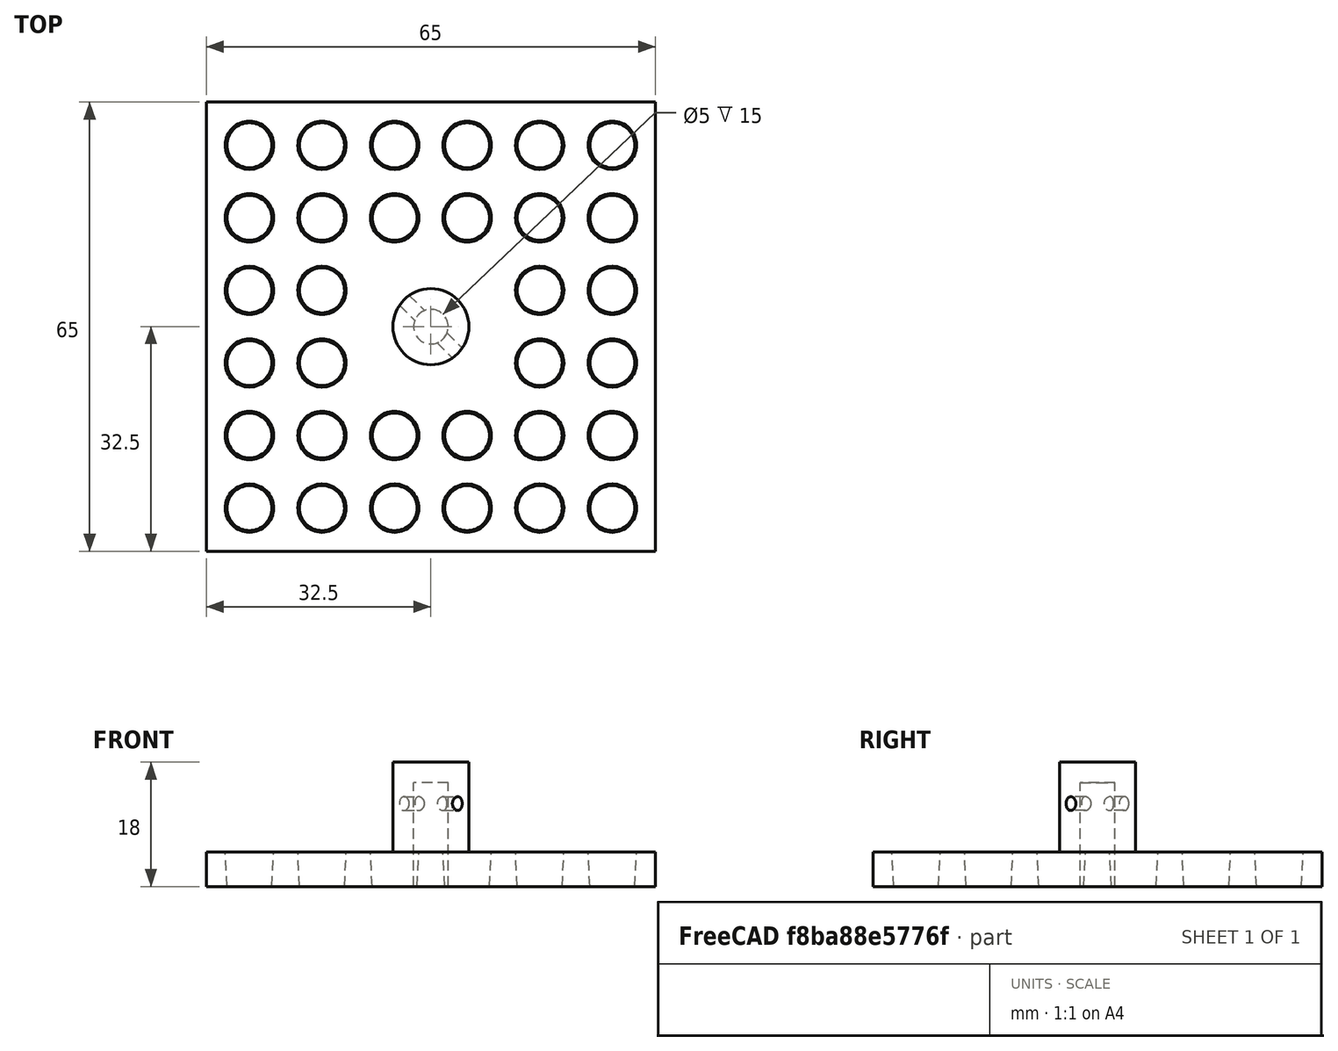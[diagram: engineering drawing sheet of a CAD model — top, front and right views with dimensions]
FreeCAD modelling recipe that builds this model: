
FCSTD DOCUMENT  (FreeCAD 0.17R13541 (Git))
Label: tip-changer-top
License: All rights reserved
LicenseURL: http://en.wikipedia.org/wiki/All_rights_reserved
objects: Part::Cut×34, Part::Cone×32, Part::Cylinder×4, Part::MultiFuse×2, Part::Box×1, Spreadsheet::Sheet×1, Mesh::Feature×1
note: 73 computed .brp shape members not serialized (recipe doc carries the construction recipe); baked Part::Feature solids carry a one-line shape summary decoded from their .brp

FEATURE [Part::Cone] Cone019  label="Kegel019"
  Angle = 360
  AttacherType = Attacher::AttachEngine3D
  Height = 5
  Placement = pos=(-5.25,15.75,78) rot=(0,0,1;0rad)
  Radius1 = 3.25
  Radius2 = 3.5
  expr: Placement.Base.y = Tabelle1.B6 / 2 - Tabelle1.B39 - Tabelle1.B37
  expr: Placement.Base.x = Tabelle1.B6 / 2 - Tabelle1.B39 - Tabelle1.B37 * 3
  expr: Placement.Base.z = Tabelle1.B33 + Tabelle1.B14
  expr: Radius2 = Tabelle1.B35 / 2
  expr: Radius1 = Tabelle1.B36 / 2
FEATURE [Part::Cylinder] Cylinder028  label="Zylinder026"
  Angle = 360
  AttacherType = Attacher::AttachEngine3D
  Height = 15
  Placement = pos=(-6,6,90) rot=(0.862856,0.357407,0.357407;1.71777rad)
  Radius = 1
FEATURE [Part::Cone] Cone018  label="Kegel018"
  Angle = 360
  AttacherType = Attacher::AttachEngine3D
  Height = 5
  Placement = pos=(5.25,26.25,78) rot=(0,0,1;0rad)
  Radius1 = 3.25
  Radius2 = 3.5
  expr: Placement.Base.y = Tabelle1.B6 / 2 - Tabelle1.B39
  expr: Placement.Base.x = Tabelle1.B6 / 2 - Tabelle1.B39 - Tabelle1.B37 * 2
  expr: Placement.Base.z = Tabelle1.B33 + Tabelle1.B14
  expr: Radius2 = Tabelle1.B35 / 2
  expr: Radius1 = Tabelle1.B36 / 2
FEATURE [Part::Cylinder] Cylinder027  label="Zylinder025"
  Angle = 360
  AttacherType = Attacher::AttachEngine3D
  Height = 3
  Placement = pos=(0,0,93) rot=(0,0,1;0rad)
  Radius = 5.5
FEATURE [Part::Cone] Cone022  label="Kegel022"
  Angle = 360
  AttacherType = Attacher::AttachEngine3D
  Height = 5
  Placement = pos=(15.75,-26.25,78) rot=(0,0,1;0rad)
  Radius1 = 3.25
  Radius2 = 3.5
  expr: Placement.Base.y = Tabelle1.B6 / 2 - Tabelle1.B39 - Tabelle1.B37 * 5
  expr: Placement.Base.x = Tabelle1.B6 / 2 - Tabelle1.B39 - Tabelle1.B37 * 1
  expr: Placement.Base.z = Tabelle1.B33 + Tabelle1.B14
  expr: Radius2 = Tabelle1.B35 / 2
  expr: Radius1 = Tabelle1.B36 / 2
FEATURE [Part::Cone] Cone021  label="Kegel021"
  Angle = 360
  AttacherType = Attacher::AttachEngine3D
  Height = 5
  Placement = pos=(5.25,-26.25,78) rot=(0,0,1;0rad)
  Radius1 = 3.25
  Radius2 = 3.5
  expr: Placement.Base.y = Tabelle1.B6 / 2 - Tabelle1.B39 - Tabelle1.B37 * 5
  expr: Placement.Base.x = Tabelle1.B6 / 2 - Tabelle1.B39 - Tabelle1.B37 * 2
  expr: Placement.Base.z = Tabelle1.B33 + Tabelle1.B14
  expr: Radius2 = Tabelle1.B35 / 2
  expr: Radius1 = Tabelle1.B36 / 2
FEATURE [Part::Cone] Cone023  label="Kegel023"
  Angle = 360
  AttacherType = Attacher::AttachEngine3D
  Height = 5
  Placement = pos=(26.25,-26.25,78) rot=(0,0,1;0rad)
  Radius1 = 3.25
  Radius2 = 3.5
  expr: Placement.Base.y = Tabelle1.B6 / 2 - Tabelle1.B39 - Tabelle1.B37 * 5
  expr: Placement.Base.x = Tabelle1.B6 / 2 - Tabelle1.B39 - Tabelle1.B37 * 0
  expr: Placement.Base.z = Tabelle1.B33 + Tabelle1.B14
  expr: Radius2 = Tabelle1.B35 / 2
  expr: Radius1 = Tabelle1.B36 / 2
FEATURE [Part::Cylinder] Cylinder020  label="Spindel001"
  Angle = 360
  AttacherType = Attacher::AttachEngine3D
  Height = 60
  Placement = pos=(0,0,33) rot=(0,0,1;0rad)
  Radius = 2.5
  expr: Placement.Base.z = Tabelle1.B33 + Tabelle1.B14 - Tabelle1.B15 + Tabelle1.B12
  expr: Height = Tabelle1.B15
FEATURE [Part::Cone] Cone020  label="Kegel020"
  Angle = 360
  AttacherType = Attacher::AttachEngine3D
  Height = 5
  Placement = pos=(5.25,15.75,78) rot=(0,0,1;0rad)
  Radius1 = 3.25
  Radius2 = 3.5
  expr: Placement.Base.y = Tabelle1.B6 / 2 - Tabelle1.B39 - Tabelle1.B37
  expr: Placement.Base.x = Tabelle1.B6 / 2 - Tabelle1.B39 - Tabelle1.B37 * 2
  expr: Placement.Base.z = Tabelle1.B33 + Tabelle1.B14
  expr: Radius2 = Tabelle1.B35 / 2
  expr: Radius1 = Tabelle1.B36 / 2
FEATURE [Part::Cone] Cone024  label="Kegel024"
  Angle = 360
  AttacherType = Attacher::AttachEngine3D
  Height = 5
  Placement = pos=(-5.25,-26.25,78) rot=(0,0,1;0rad)
  Radius1 = 3.25
  Radius2 = 3.5
  expr: Placement.Base.y = Tabelle1.B6 / 2 - Tabelle1.B39 - Tabelle1.B37 * 5
  expr: Placement.Base.x = Tabelle1.B6 / 2 - Tabelle1.B39 - Tabelle1.B37 * 3
  expr: Placement.Base.z = Tabelle1.B33 + Tabelle1.B14
  expr: Radius2 = Tabelle1.B35 / 2
  expr: Radius1 = Tabelle1.B36 / 2
FEATURE [Part::Cone] Cone029  label="Kegel029"
  Angle = 360
  AttacherType = Attacher::AttachEngine3D
  Height = 5
  Placement = pos=(-26.25,5.25,78) rot=(0,0,1;0rad)
  Radius1 = 3.25
  Radius2 = 3.5
  expr: Placement.Base.y = Tabelle1.B6 / 2 - Tabelle1.B39 - Tabelle1.B37 * 2
  expr: Placement.Base.x = Tabelle1.B6 / 2 - Tabelle1.B39 - Tabelle1.B37 * 5
  expr: Placement.Base.z = Tabelle1.B33 + Tabelle1.B14
  expr: Radius2 = Tabelle1.B35 / 2
  expr: Radius1 = Tabelle1.B36 / 2
FEATURE [Part::Cone] Cone030  label="Kegel030"
  Angle = 360
  AttacherType = Attacher::AttachEngine3D
  Height = 5
  Placement = pos=(-26.25,15.75,78) rot=(0,0,1;0rad)
  Radius1 = 3.25
  Radius2 = 3.5
  expr: Placement.Base.y = Tabelle1.B6 / 2 - Tabelle1.B39 - Tabelle1.B37 * 1
  expr: Placement.Base.x = Tabelle1.B6 / 2 - Tabelle1.B39 - Tabelle1.B37 * 5
  expr: Placement.Base.z = Tabelle1.B33 + Tabelle1.B14
  expr: Radius2 = Tabelle1.B35 / 2
  expr: Radius1 = Tabelle1.B36 / 2
FEATURE [Part::Cone] Cone027  label="Kegel027"
  Angle = 360
  AttacherType = Attacher::AttachEngine3D
  Height = 5
  Placement = pos=(-26.25,-15.75,78) rot=(0,0,1;0rad)
  Radius1 = 3.25
  Radius2 = 3.5
  expr: Placement.Base.y = Tabelle1.B6 / 2 - Tabelle1.B39 - Tabelle1.B37 * 4
  expr: Placement.Base.x = Tabelle1.B6 / 2 - Tabelle1.B39 - Tabelle1.B37 * 5
  expr: Placement.Base.z = Tabelle1.B33 + Tabelle1.B14
  expr: Radius2 = Tabelle1.B35 / 2
  expr: Radius1 = Tabelle1.B36 / 2
FEATURE [Part::Cone] Cone025  label="Kegel025"
  Angle = 360
  AttacherType = Attacher::AttachEngine3D
  Height = 5
  Placement = pos=(-15.75,-26.25,78) rot=(0,0,1;0rad)
  Radius1 = 3.25
  Radius2 = 3.5
  expr: Placement.Base.y = Tabelle1.B6 / 2 - Tabelle1.B39 - Tabelle1.B37 * 5
  expr: Placement.Base.x = Tabelle1.B6 / 2 - Tabelle1.B39 - Tabelle1.B37 * 4
  expr: Placement.Base.z = Tabelle1.B33 + Tabelle1.B14
  expr: Radius2 = Tabelle1.B35 / 2
  expr: Radius1 = Tabelle1.B36 / 2
FEATURE [Part::Cone] Cone028  label="Kegel028"
  Angle = 360
  AttacherType = Attacher::AttachEngine3D
  Height = 5
  Placement = pos=(-26.25,-5.25,78) rot=(0,0,1;0rad)
  Radius1 = 3.25
  Radius2 = 3.5
  expr: Placement.Base.y = Tabelle1.B6 / 2 - Tabelle1.B39 - Tabelle1.B37 * 3
  expr: Placement.Base.x = Tabelle1.B6 / 2 - Tabelle1.B39 - Tabelle1.B37 * 5
  expr: Placement.Base.z = Tabelle1.B33 + Tabelle1.B14
  expr: Radius2 = Tabelle1.B35 / 2
  expr: Radius1 = Tabelle1.B36 / 2
FEATURE [Part::Cone] Cone031  label="Kegel031"
  Angle = 360
  AttacherType = Attacher::AttachEngine3D
  Height = 5
  Placement = pos=(-26.25,26.25,78) rot=(0,0,1;0rad)
  Radius1 = 3.25
  Radius2 = 3.5
  expr: Placement.Base.y = Tabelle1.B6 / 2 - Tabelle1.B39 - Tabelle1.B37 * 0
  expr: Placement.Base.x = Tabelle1.B6 / 2 - Tabelle1.B39 - Tabelle1.B37 * 5
  expr: Placement.Base.z = Tabelle1.B33 + Tabelle1.B14
  expr: Radius2 = Tabelle1.B35 / 2
  expr: Radius1 = Tabelle1.B36 / 2
FEATURE [Part::Cone] Cone026  label="Kegel026"
  Angle = 360
  AttacherType = Attacher::AttachEngine3D
  Height = 5
  Placement = pos=(-26.25,-26.25,78) rot=(0,0,1;0rad)
  Radius1 = 3.25
  Radius2 = 3.5
  expr: Placement.Base.y = Tabelle1.B6 / 2 - Tabelle1.B39 - Tabelle1.B37 * 5
  expr: Placement.Base.x = Tabelle1.B6 / 2 - Tabelle1.B39 - Tabelle1.B37 * 5
  expr: Placement.Base.z = Tabelle1.B33 + Tabelle1.B14
  expr: Radius2 = Tabelle1.B35 / 2
  expr: Radius1 = Tabelle1.B36 / 2
FEATURE [Part::Cone] Cone014  label="Kegel014"
  Angle = 360
  AttacherType = Attacher::AttachEngine3D
  Height = 5
  Placement = pos=(-15.75,5.25,78) rot=(0,0,1;0rad)
  Radius1 = 3.25
  Radius2 = 3.5
  expr: Placement.Base.y = Tabelle1.B6 / 2 - Tabelle1.B39 - Tabelle1.B37 * 2
  expr: Placement.Base.x = Tabelle1.B6 / 2 - Tabelle1.B39 - Tabelle1.B37 * 4
  expr: Placement.Base.z = Tabelle1.B33 + Tabelle1.B14
  expr: Radius2 = Tabelle1.B35 / 2
  expr: Radius1 = Tabelle1.B36 / 2
FEATURE [Part::Cone] Cone001  label="Kegel001"
  Angle = 360
  AttacherType = Attacher::AttachEngine3D
  Height = 5
  Placement = pos=(26.25,15.75,78) rot=(0,0,1;0rad)
  Radius1 = 3.25
  Radius2 = 3.5
  expr: Placement.Base.y = Tabelle1.B6 / 2 - Tabelle1.B39 - Tabelle1.B37
  expr: Placement.Base.x = Tabelle1.B6 / 2 - Tabelle1.B39
  expr: Placement.Base.z = Tabelle1.B33 + Tabelle1.B14
  expr: Radius2 = Tabelle1.B35 / 2
  expr: Radius1 = Tabelle1.B36 / 2
FEATURE [Part::Cone] Cone015  label="Kegel015"
  Angle = 360
  AttacherType = Attacher::AttachEngine3D
  Height = 5
  Placement = pos=(-15.75,15.75,78) rot=(0,0,1;0rad)
  Radius1 = 3.25
  Radius2 = 3.5
  expr: Placement.Base.y = Tabelle1.B6 / 2 - Tabelle1.B39 - Tabelle1.B37
  expr: Placement.Base.x = Tabelle1.B6 / 2 - Tabelle1.B39 - Tabelle1.B37 * 4
  expr: Placement.Base.z = Tabelle1.B33 + Tabelle1.B14
  expr: Radius2 = Tabelle1.B35 / 2
  expr: Radius1 = Tabelle1.B36 / 2
FEATURE [Part::Box] Box001  label="Platte"
  AttacherType = Attacher::AttachEngine3D
  Height = 5
  Length = 65
  Placement = pos=(-32.5,-32.5,78) rot=(0,0,1;0rad)
  Width = 65
  expr: Length = Tabelle1.B6
  expr: Placement.Base.z = Tabelle1.B33 + Tabelle1.B14
  expr: Placement.Base.y = -Tabelle1.B6 / 2
  expr: Placement.Base.x = -Tabelle1.B6 / 2
  expr: Width = Tabelle1.B6
FEATURE [Part::Cone] Cone006  label="Kegel006"
  Angle = 360
  AttacherType = Attacher::AttachEngine3D
  Height = 5
  Placement = pos=(15.75,-5.25,78) rot=(0,0,1;0rad)
  Radius1 = 3.25
  Radius2 = 3.5
  expr: Placement.Base.y = Tabelle1.B6 / 2 - Tabelle1.B39 - Tabelle1.B37 * 3
  expr: Placement.Base.x = Tabelle1.B6 / 2 - Tabelle1.B39 - Tabelle1.B37
  expr: Placement.Base.z = Tabelle1.B33 + Tabelle1.B14
  expr: Radius2 = Tabelle1.B35 / 2
  expr: Radius1 = Tabelle1.B36 / 2
FEATURE [Part::Cone] Cone016  label="Kegel016"
  Angle = 360
  AttacherType = Attacher::AttachEngine3D
  Height = 5
  Placement = pos=(-15.75,26.25,78) rot=(0,0,1;0rad)
  Radius1 = 3.25
  Radius2 = 3.5
  expr: Placement.Base.y = Tabelle1.B6 / 2 - Tabelle1.B39
  expr: Placement.Base.x = Tabelle1.B6 / 2 - Tabelle1.B39 - Tabelle1.B37 * 4
  expr: Placement.Base.z = Tabelle1.B33 + Tabelle1.B14
  expr: Radius2 = Tabelle1.B35 / 2
  expr: Radius1 = Tabelle1.B36 / 2
FEATURE [Part::Cone] Cone010  label="Kegel010"
  Angle = 360
  AttacherType = Attacher::AttachEngine3D
  Height = 5
  Placement = pos=(5.25,-15.75,78) rot=(0,0,1;0rad)
  Radius1 = 3.25
  Radius2 = 3.5
  expr: Placement.Base.y = Tabelle1.B6 / 2 - Tabelle1.B39 - Tabelle1.B37 * 4
  expr: Placement.Base.x = Tabelle1.B6 / 2 - Tabelle1.B39 - Tabelle1.B37 * 2
  expr: Placement.Base.z = Tabelle1.B33 + Tabelle1.B14
  expr: Radius2 = Tabelle1.B35 / 2
  expr: Radius1 = Tabelle1.B36 / 2
FEATURE [Part::Cylinder] Cylinder019  label="Zylinder018"
  Angle = 360
  AttacherType = Attacher::AttachEngine3D
  Height = 10
  Placement = pos=(0,0,83) rot=(0,0,1;0rad)
  Radius = 5.5
  expr: Placement.Base.z = Tabelle1.B33 + Tabelle1.B14 + Tabelle1.B7
  expr: Height = Tabelle1.B8
  expr: Radius = Tabelle1.B11 / 2 + Tabelle1.B19
FEATURE [Part::Cone] Cone011  label="Kegel011"
  Angle = 360
  AttacherType = Attacher::AttachEngine3D
  Height = 5
  Placement = pos=(-5.25,-15.75,78) rot=(0,0,1;0rad)
  Radius1 = 3.25
  Radius2 = 3.5
  expr: Placement.Base.y = Tabelle1.B6 / 2 - Tabelle1.B39 - Tabelle1.B37 * 4
  expr: Placement.Base.x = Tabelle1.B6 / 2 - Tabelle1.B39 - Tabelle1.B37 * 3
  expr: Placement.Base.z = Tabelle1.B33 + Tabelle1.B14
  expr: Radius2 = Tabelle1.B35 / 2
  expr: Radius1 = Tabelle1.B36 / 2
FEATURE [Part::Cone] Cone017  label="Kegel017"
  Angle = 360
  AttacherType = Attacher::AttachEngine3D
  Height = 5
  Placement = pos=(-5.25,26.25,78) rot=(0,0,1;0rad)
  Radius1 = 3.25
  Radius2 = 3.5
  expr: Placement.Base.y = Tabelle1.B6 / 2 - Tabelle1.B39
  expr: Placement.Base.x = Tabelle1.B6 / 2 - Tabelle1.B39 - Tabelle1.B37 * 3
  expr: Placement.Base.z = Tabelle1.B33 + Tabelle1.B14
  expr: Radius2 = Tabelle1.B35 / 2
  expr: Radius1 = Tabelle1.B36 / 2
FEATURE [Part::Cone] Cone007  label="Kegel007"
  Angle = 360
  AttacherType = Attacher::AttachEngine3D
  Height = 5
  Placement = pos=(15.75,5.25,78) rot=(0,0,1;0rad)
  Radius1 = 3.25
  Radius2 = 3.5
  expr: Placement.Base.y = Tabelle1.B6 / 2 - Tabelle1.B39 - Tabelle1.B37 * 2
  expr: Placement.Base.x = Tabelle1.B6 / 2 - Tabelle1.B39 - Tabelle1.B37
  expr: Placement.Base.z = Tabelle1.B33 + Tabelle1.B14
  expr: Radius2 = Tabelle1.B35 / 2
  expr: Radius1 = Tabelle1.B36 / 2
FEATURE [Part::Cone] Cone008  label="Kegel008"
  Angle = 360
  AttacherType = Attacher::AttachEngine3D
  Height = 5
  Placement = pos=(15.75,15.75,78) rot=(0,0,1;0rad)
  Radius1 = 3.25
  Radius2 = 3.5
  expr: Placement.Base.y = Tabelle1.B6 / 2 - Tabelle1.B39 - Tabelle1.B37
  expr: Placement.Base.x = Tabelle1.B6 / 2 - Tabelle1.B39 - Tabelle1.B37
  expr: Placement.Base.z = Tabelle1.B33 + Tabelle1.B14
  expr: Radius2 = Tabelle1.B35 / 2
  expr: Radius1 = Tabelle1.B36 / 2
FEATURE [Part::Cone] Cone005  label="Kegel005"
  Angle = 360
  AttacherType = Attacher::AttachEngine3D
  Height = 5
  Placement = pos=(26.25,-15.75,78) rot=(0,0,1;0rad)
  Radius1 = 3.25
  Radius2 = 3.5
  expr: Placement.Base.y = Tabelle1.B6 / 2 - Tabelle1.B37 * 4 - Tabelle1.B39
  expr: Placement.Base.x = Tabelle1.B6 / 2 - Tabelle1.B39
  expr: Placement.Base.z = Tabelle1.B33 + Tabelle1.B14
  expr: Radius2 = Tabelle1.B35 / 2
  expr: Radius1 = Tabelle1.B36 / 2
FEATURE [Part::Cone] Cone009  label="Kegel009"
  Angle = 360
  AttacherType = Attacher::AttachEngine3D
  Height = 5
  Placement = pos=(15.75,26.25,78) rot=(0,0,1;0rad)
  Radius1 = 3.25
  Radius2 = 3.5
  expr: Placement.Base.y = Tabelle1.B6 / 2 - Tabelle1.B39
  expr: Placement.Base.x = Tabelle1.B6 / 2 - Tabelle1.B39 - Tabelle1.B37
  expr: Placement.Base.z = Tabelle1.B33 + Tabelle1.B14
  expr: Radius2 = Tabelle1.B35 / 2
  expr: Radius1 = Tabelle1.B36 / 2
FEATURE [Part::Cone] Cone013  label="Kegel013"
  Angle = 360
  AttacherType = Attacher::AttachEngine3D
  Height = 5
  Placement = pos=(-15.75,-5.25,78) rot=(0,0,1;0rad)
  Radius1 = 3.25
  Radius2 = 3.5
  expr: Placement.Base.y = Tabelle1.B6 / 2 - Tabelle1.B39 - Tabelle1.B37 * 3
  expr: Placement.Base.x = Tabelle1.B6 / 2 - Tabelle1.B39 - Tabelle1.B37 * 4
  expr: Placement.Base.z = Tabelle1.B33 + Tabelle1.B14
  expr: Radius2 = Tabelle1.B35 / 2
  expr: Radius1 = Tabelle1.B36 / 2
FEATURE [Part::Cone] Cone  label="Kegel"
  Angle = 360
  AttacherType = Attacher::AttachEngine3D
  Height = 5
  Placement = pos=(26.25,26.25,78) rot=(0,0,1;0rad)
  Radius1 = 3.25
  Radius2 = 3.5
  expr: Placement.Base.y = Tabelle1.B6 / 2 - Tabelle1.B39
  expr: Placement.Base.x = Tabelle1.B6 / 2 - Tabelle1.B39
  expr: Placement.Base.z = Tabelle1.B33 + Tabelle1.B14
  expr: Radius2 = Tabelle1.B35 / 2
  expr: Radius1 = Tabelle1.B36 / 2
FEATURE [Part::Cut] Cut008
  Base = -> Box001
  Tool = -> Cone
FEATURE [Part::Cut] Cut009
  Base = -> Cut008
  Tool = -> Cone023
FEATURE [Part::Cut] Cut010
  Base = -> Cut009
  Tool = -> Cone022
FEATURE [Part::Cut] Cut011
  Base = -> Cut010
  Tool = -> Cone021
FEATURE [Part::Cone] Cone003  label="Kegel003"
  Angle = 360
  AttacherType = Attacher::AttachEngine3D
  Height = 5
  Placement = pos=(26.25,-5.25,78) rot=(0,0,1;0rad)
  Radius1 = 3.25
  Radius2 = 3.5
  expr: Placement.Base.y = Tabelle1.B6 / 2 - Tabelle1.B39 - Tabelle1.B37 * 3
  expr: Placement.Base.x = Tabelle1.B6 / 2 - Tabelle1.B39
  expr: Placement.Base.z = Tabelle1.B33 + Tabelle1.B14
  expr: Radius2 = Tabelle1.B35 / 2
  expr: Radius1 = Tabelle1.B36 / 2
FEATURE [Part::Cone] Cone002  label="Kegel002"
  Angle = 360
  AttacherType = Attacher::AttachEngine3D
  Height = 5
  Placement = pos=(26.25,5.25,78) rot=(0,0,1;0rad)
  Radius1 = 3.25
  Radius2 = 3.5
  expr: Placement.Base.y = Tabelle1.B6 / 2 - Tabelle1.B39 - Tabelle1.B37 * 2
  expr: Placement.Base.x = Tabelle1.B6 / 2 - Tabelle1.B39
  expr: Placement.Base.z = Tabelle1.B33 + Tabelle1.B14
  expr: Radius2 = Tabelle1.B35 / 2
  expr: Radius1 = Tabelle1.B36 / 2
FEATURE [Part::Cone] Cone012  label="Kegel012"
  Angle = 360
  AttacherType = Attacher::AttachEngine3D
  Height = 5
  Placement = pos=(-15.75,-15.75,78) rot=(0,0,1;0rad)
  Radius1 = 3.25
  Radius2 = 3.5
  expr: Placement.Base.y = Tabelle1.B6 / 2 - Tabelle1.B39 - Tabelle1.B37 * 4
  expr: Placement.Base.x = Tabelle1.B6 / 2 - Tabelle1.B39 - Tabelle1.B37 * 4
  expr: Placement.Base.z = Tabelle1.B33 + Tabelle1.B14
  expr: Radius2 = Tabelle1.B35 / 2
  expr: Radius1 = Tabelle1.B36 / 2
FEATURE [Part::Cone] Cone004  label="Kegel004"
  Angle = 360
  AttacherType = Attacher::AttachEngine3D
  Height = 5
  Placement = pos=(15.75,-15.75,78) rot=(0,0,1;0rad)
  Radius1 = 3.25
  Radius2 = 3.5
  expr: Placement.Base.y = Tabelle1.B6 / 2 - Tabelle1.B39 - Tabelle1.B37 * 4
  expr: Placement.Base.x = Tabelle1.B6 / 2 - Tabelle1.B39 - Tabelle1.B37
  expr: Placement.Base.z = Tabelle1.B33 + Tabelle1.B14
  expr: Radius2 = Tabelle1.B35 / 2
  expr: Radius1 = Tabelle1.B36 / 2
FEATURE [Part::Cut] Cut012
  Base = -> Cut011
  Tool = -> Cone020
FEATURE [Part::Cut] Cut013
  Base = -> Cut012
  Tool = -> Cone019
FEATURE [Part::Cut] Cut014
  Base = -> Cut013
  Tool = -> Cone018
FEATURE [Part::Cut] Cut015
  Base = -> Cut014
  Tool = -> Cone017
FEATURE [Part::Cut] Cut016
  Base = -> Cut015
  Tool = -> Cone016
FEATURE [Part::Cut] Cut017
  Base = -> Cut016
  Tool = -> Cone015
FEATURE [Part::Cut] Cut018
  Base = -> Cut017
  Tool = -> Cone014
FEATURE [Part::Cut] Cut019
  Base = -> Cut018
  Tool = -> Cone013
FEATURE [Part::Cut] Cut020
  Base = -> Cut019
  Tool = -> Cone012
FEATURE [Part::Cut] Cut021
  Base = -> Cut020
  Tool = -> Cone011
FEATURE [Part::Cut] Cut022
  Base = -> Cut021
  Tool = -> Cone010
FEATURE [Part::Cut] Cut023
  Base = -> Cut022
  Tool = -> Cone009
FEATURE [Part::Cut] Cut024
  Base = -> Cut023
  Tool = -> Cone008
FEATURE [Part::Cut] Cut025
  Base = -> Cut024
  Tool = -> Cone007
FEATURE [Part::Cut] Cut026
  Base = -> Cut025
  Tool = -> Cone006
FEATURE [Part::Cut] Cut027
  Base = -> Cut026
  Tool = -> Cone005
FEATURE [Part::Cut] Cut028
  Base = -> Cut027
  Tool = -> Cone004
FEATURE [Part::Cut] Cut029
  Base = -> Cut028
  Tool = -> Cone003
FEATURE [Part::Cut] Cut030
  Base = -> Cut029
  Tool = -> Cone002
FEATURE [Part::Cut] Cut031
  Base = -> Cut030
  Tool = -> Cone001
FEATURE [Part::MultiFuse] Fusion
  Shapes = -> [Cut031,Cylinder019]
FEATURE [Part::Cut] Cut032
  Base = -> Fusion
  Tool = -> Cylinder020
FEATURE [Part::MultiFuse] Fusion002  label="top"
  Shapes = -> [Cut032,Cylinder027]
FEATURE [Part::Cut] Cut042  label="Top"
  Base = -> Fusion002
  Tool = -> Cylinder028
FEATURE [Part::Cut] Cut048
  Base = -> Cut042
  Tool = -> Cone024
FEATURE [Part::Cut] Cut049
  Base = -> Cut048
  Tool = -> Cone031
FEATURE [Part::Cut] Cut050
  Base = -> Cut049
  Tool = -> Cone030
FEATURE [Part::Cut] Cut051
  Base = -> Cut050
  Tool = -> Cone029
FEATURE [Part::Cut] Cut052
  Base = -> Cut051
  Tool = -> Cone028
FEATURE [Part::Cut] Cut053
  Base = -> Cut052
  Tool = -> Cone027
FEATURE [Part::Cut] Cut054
  Base = -> Cut053
  Tool = -> Cone026
FEATURE [Part::Cut] Cut055  label="tip-changer-top"
  Base = -> Cut054
  Tool = -> Cone025
FEATURE [Spreadsheet::Sheet] Tabelle1
  cells = A1=Abstand Pip/Boden; B1=65; A3=Toleranz; B3=0.20000000000000001; A5=Teller; A6=Breite/Länge; B6=65; A7=Dicke; B7=5; A8=Befestigung höhe; B8=10; A10=Achse; A11=Durchmesser; B11=5; A12=Teller Befestigung; B12==B7 + B8; A13=Führung Länge; B13=40; C13=Wandstärke; D13=5; A14=Freiraum; B14=5; A15=Länge; B15==B14 + B13 + B12; A17=Feder; A18=Hülse durchmesser; B18=3.6000000000000001; A19=Hülse Wanddicke; B19=3; A20=L0; B20=25; A21=delta L; B21=3; A22=Spannmutter; A23=Höhe; B23=10; A24=Durchmesser Pitch; B24=20; A25=min Abstand Boden; B25=5; A28=min Oberkante Platte; B28==B25 + B23 + B20 + B19 + B13 + B7; A30=Gehäuse; A31=Wandstärke; B31=5; A32=Durchmesser; B32==B24 + 2 * B31; A33=Höhe; B33==B25 + B20 + B19 + B13; A35=Spitze d1; B35=7; A36=Spitze d2; B36=6.5; A37=Raster; B37=10.5; A38=Anzahl x/y; B38=6; A39=offset; B39==(Tabelle1.B6 - ((Tabelle1.B38 - 1) * Tabelle1.B37 + Tabelle1.B35)) / 2 + Tabelle1.B35 / 2
FEATURE [Mesh::Feature] Mesh  label="tip-changer-top (Meshed)"
